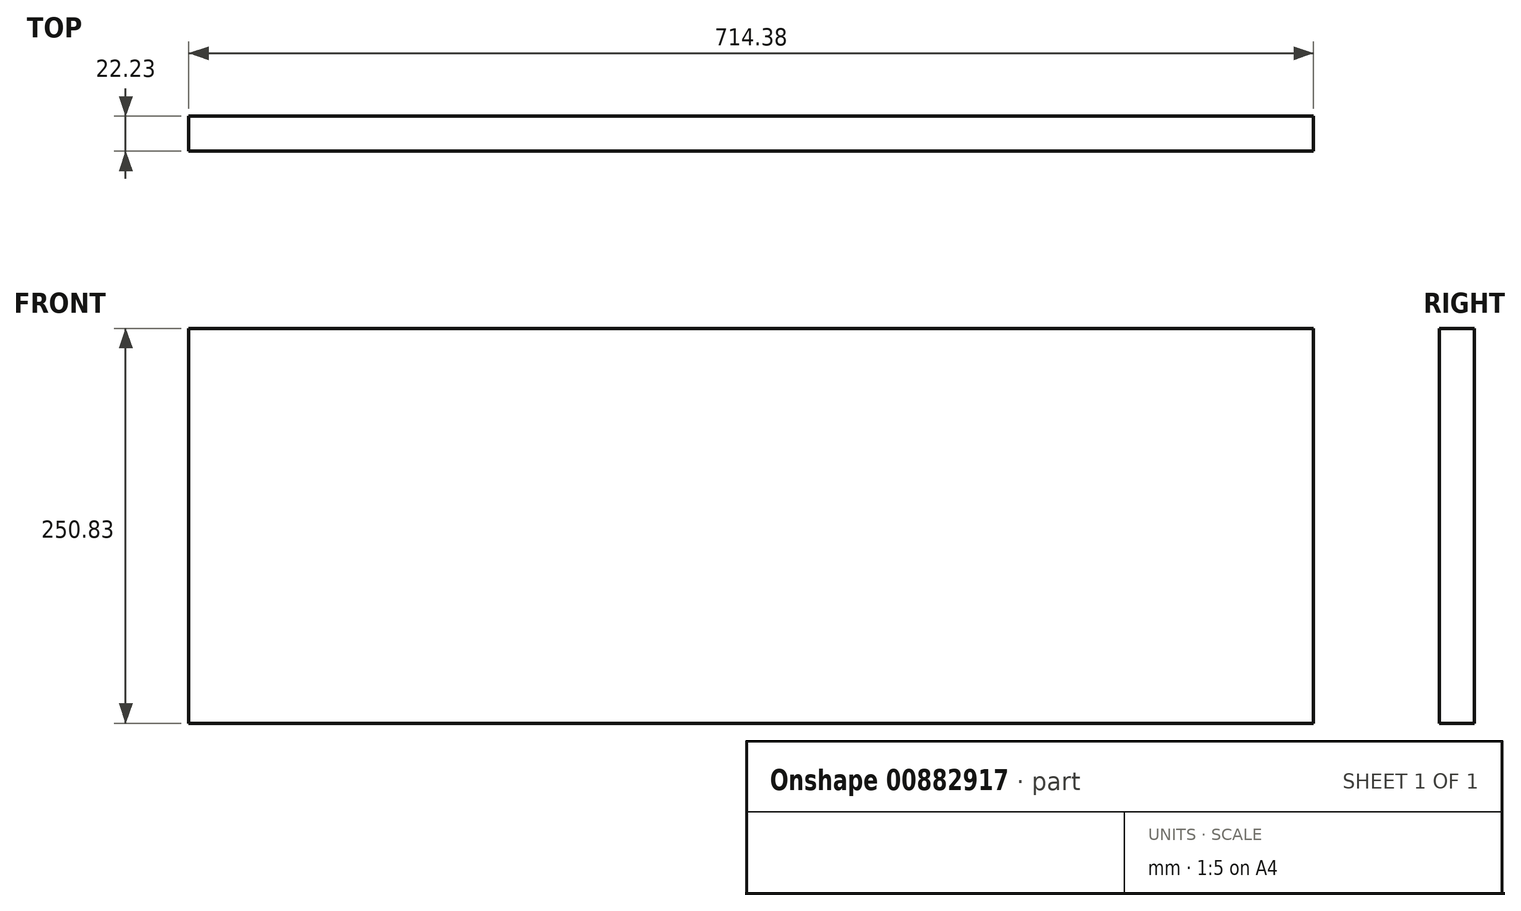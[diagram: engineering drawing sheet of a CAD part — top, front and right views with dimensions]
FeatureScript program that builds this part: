
annotation { "Feature Type Name" : "Feature", "Feature Type Description" : "" }
export const myFeature = defineFeature(function(context is Context, id is Id, definition is map)
    precondition{}
    {
        {
            var Q0;
            Q0=qCreatedBy(makeId("Front.planeOp"),FACE);
            var sketch = newSketch(context, id + "F0", { "sketchPlane" : qUnion([Q0])});
            skLineSegment(sketch, "E0.bottom", {"start": v(0, 0) * mm, "end": v(714.38, 0) * mm});
            skLineSegment(sketch, "E0.top", {"start": v(0, -250.82) * mm, "end": v(714.38, -250.82) * mm});
            skLineSegment(sketch, "E0.left", {"start": v(0, 0) * mm, "end": v(0, -250.82) * mm});
            skLineSegment(sketch, "E0.right", {"start": v(714.38, 0) * mm, "end": v(714.38, -250.82) * mm});
            skSolve(sketch);
        }
        {
            var Q0;
            Q0=makeQuery(id+"F0.imprint","IMPRINT",FACE,{"disambiguationData":[TD([[makeQuery(id+"F0.imprint","IMPRINT",EDGE,{"derivedFrom":sQuery(id+"F0.wireOp",EDGE,"E0.bottom")}),-1.0]])]});
            extrude(context, id + "F1", {"entities" : qUnion([Q0]), "depth" : 22.22 * mm, "offsetDistance" : 25.4 * mm});
        }
    });
